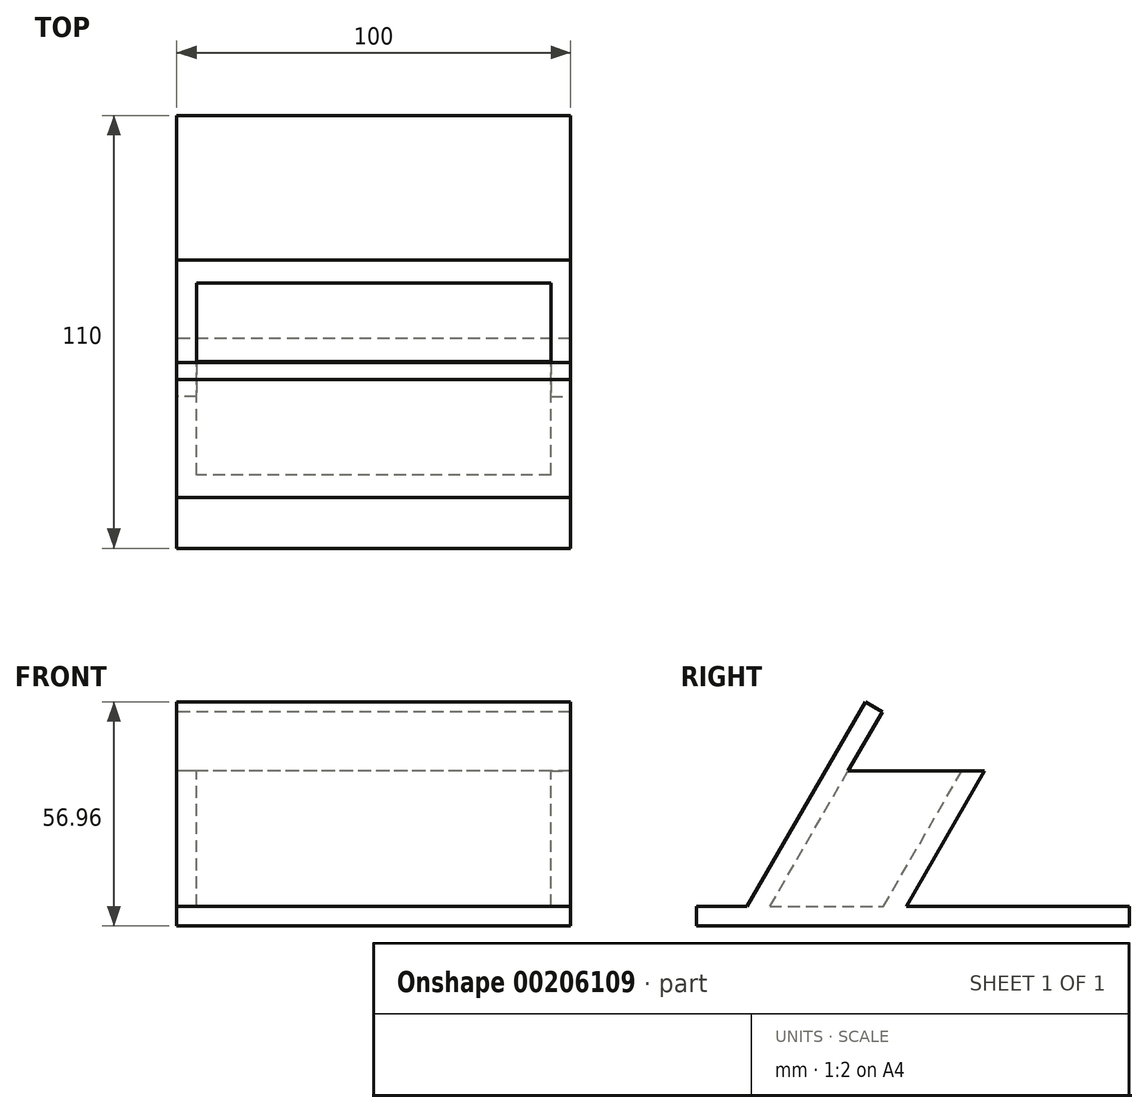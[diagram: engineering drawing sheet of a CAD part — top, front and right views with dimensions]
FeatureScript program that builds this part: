
annotation { "Feature Type Name" : "Feature", "Feature Type Description" : "" }
export const myFeature = defineFeature(function(context is Context, id is Id, definition is map)
    precondition{}
    {
        {
            var Q0;
            Q0=qCreatedBy(makeId("Right.planeOp"),FACE);
            var sketch = newSketch(context, id + "F0", { "sketchPlane" : qUnion([Q0])});
            skLineSegment(sketch, "E0", {"start": v(0, 0) * mm, "end": v(100, 0) * mm});
            skLineSegment(sketch, "E1", {"start": v(2.89, 5) * mm, "end": v(32.89, 56.96) * mm});
            skPoint(sketch, "E2.visualSharp", {"position": v(0, 0) * mm});
            skLineSegment(sketch, "E3.0", {"start": v(8.66, 5) * mm, "end": v(37.22, 54.46) * mm});
            skLineSegment(sketch, "E3.2", {"start": v(8.66, 5) * mm, "end": v(37.53, 5) * mm});
            skLineSegment(sketch, "E4", {"start": v(100, 5) * mm, "end": v(100, 0) * mm});
            skLineSegment(sketch, "E5", {"start": v(32.89, 56.96) * mm, "end": v(37.22, 54.46) * mm});
            skLineSegment(sketch, "E6", {"start": v(0, 0) * mm, "end": v(0, 5) * mm});
            skLineSegment(sketch, "E7", {"start": v(0, 5) * mm, "end": v(2.89, 5) * mm});
            skLineSegment(sketch, "E8.trimOffspring", {"start": v(43.3, 5) * mm, "end": v(63.2, 39.46) * mm});
            skLineSegment(sketch, "E9.trimOffspring", {"start": v(37.53, 5) * mm, "end": v(57.42, 39.46) * mm});
            skLineSegment(sketch, "E10.trimOffspring", {"start": v(43.3, 5) * mm, "end": v(100, 5) * mm});
            skLineSegment(sketch, "E11", {"start": v(63.2, 39.46) * mm, "end": v(57.42, 39.46) * mm});
            skSolve(sketch);
        }
        {
            var Q0;
            Q0=makeQuery(id+"F0.imprint","IMPRINT",FACE,{"disambiguationData":[TD([[makeQuery(id+"F0.imprint","IMPRINT",EDGE,{"derivedFrom":sQuery(id+"F0.wireOp",EDGE,"E0")}),1.0]])]});
            extrude(context, id + "F1", {"entities" : qUnion([Q0]), "depth" : 100 * mm});
        }
        {
            var Q0;
            Q0=makeQuery(id+"F1.opExtrude","CAP_FACE",FACE,{"disambiguationData":[OSD([sQuery(id+"F0.wireOp",EDGE,"E0"),sQuery(id+"F0.wireOp",EDGE,"E3.0"),sQuery(id+"F0.wireOp",EDGE,"E3.2"),sQuery(id+"F0.wireOp",EDGE,"E4"),sQuery(id+"F0.wireOp",EDGE,"E5"),sQuery(id+"F0.wireOp",EDGE,"E1"),sQuery(id+"F0.wireOp",EDGE,"E6"),sQuery(id+"F0.wireOp",EDGE,"E7"),sQuery(id+"F0.wireOp",EDGE,"E8.trimOffspring"),sQuery(id+"F0.wireOp",EDGE,"E9.trimOffspring"),sQuery(id+"F0.wireOp",EDGE,"E10.trimOffspring"),sQuery(id+"F0.wireOp",EDGE,"E11")])],"isStart":false});
            var sketch = newSketch(context, id + "F2", { "sketchPlane" : qUnion([Q0])});
            skLineSegment(sketch, "E12", {"start": v(57.42, 39.46) * mm, "end": v(28.56, 39.46) * mm});
            skLineSegment(sketch, "E13", {"start": v(28.56, 39.46) * mm, "end": v(8.66, 5) * mm});
            skLineSegment(sketch, "E14", {"start": v(8.66, 5) * mm, "end": v(37.53, 5) * mm});
            skLineSegment(sketch, "E15", {"start": v(37.53, 5) * mm, "end": v(57.42, 39.46) * mm});
            skSolve(sketch);
        }
        {
            var Q0;
            Q0=makeQuery(id+"F2.imprint","IMPRINT",FACE,{"disambiguationData":[TD([[makeQuery(id+"F2.imprint","IMPRINT",EDGE,{"derivedFrom":sQuery(id+"F2.wireOp",EDGE,"E12")}),1.0]])]});
            extrude(context, id + "F3", {"entities" : qUnion([Q0]), "operationType" : NewBodyOperationType.ADD, "oppositeDirection" : true, "depth" : 5 * mm});
        }
        {
            var Q0;
            Q0=makeQuery(id+"F1.opExtrude","CAP_FACE",FACE,{"disambiguationData":[OSD([sQuery(id+"F0.wireOp",EDGE,"E0"),sQuery(id+"F0.wireOp",EDGE,"E3.0"),sQuery(id+"F0.wireOp",EDGE,"E3.2"),sQuery(id+"F0.wireOp",EDGE,"E4"),sQuery(id+"F0.wireOp",EDGE,"E5"),sQuery(id+"F0.wireOp",EDGE,"E1"),sQuery(id+"F0.wireOp",EDGE,"E6"),sQuery(id+"F0.wireOp",EDGE,"E7"),sQuery(id+"F0.wireOp",EDGE,"E8.trimOffspring"),sQuery(id+"F0.wireOp",EDGE,"E9.trimOffspring"),sQuery(id+"F0.wireOp",EDGE,"E10.trimOffspring"),sQuery(id+"F0.wireOp",EDGE,"E11")])],"isStart":true});
            var sketch = newSketch(context, id + "F4", { "sketchPlane" : qUnion([Q0])});
            skLineSegment(sketch, "E16", {"start": v(-57.42, 39.46) * mm, "end": v(-28.56, 39.46) * mm});
            skSolve(sketch);
        }
        {
            var Q0;
            Q0 = qSketchRegion(id + "F4", true);
            var Q1;
            {var subQ0=sQuery(id+"F4.wireOp",EDGE,"E16");Q1=makeQuery(id+"F4.imprint","IMPRINT",FACE,{"disambiguationData":[TD([[makeQuery(id+"F4.imprint","IMPRINT",EDGE,{"derivedFrom":subQ0}),-1.0]])]});}
            extrude(context, id + "F5", {"entities" : qUnion([Q0, Q1]), "operationType" : NewBodyOperationType.ADD, "oppositeDirection" : true, "depth" : 5 * mm});
        }
        {
            var Q0;
            Q0=makeQuery(id+"F1.opExtrude","SWEPT_FACE",FACE,{"disambiguationData":[OSD([sQuery(id+"F0.wireOp",EDGE,"E6")])]});
            extrude(context, id + "F6", {"entities" : qUnion([Q0]), "operationType" : NewBodyOperationType.ADD, "depth" : 10 * mm});
        }
    });
